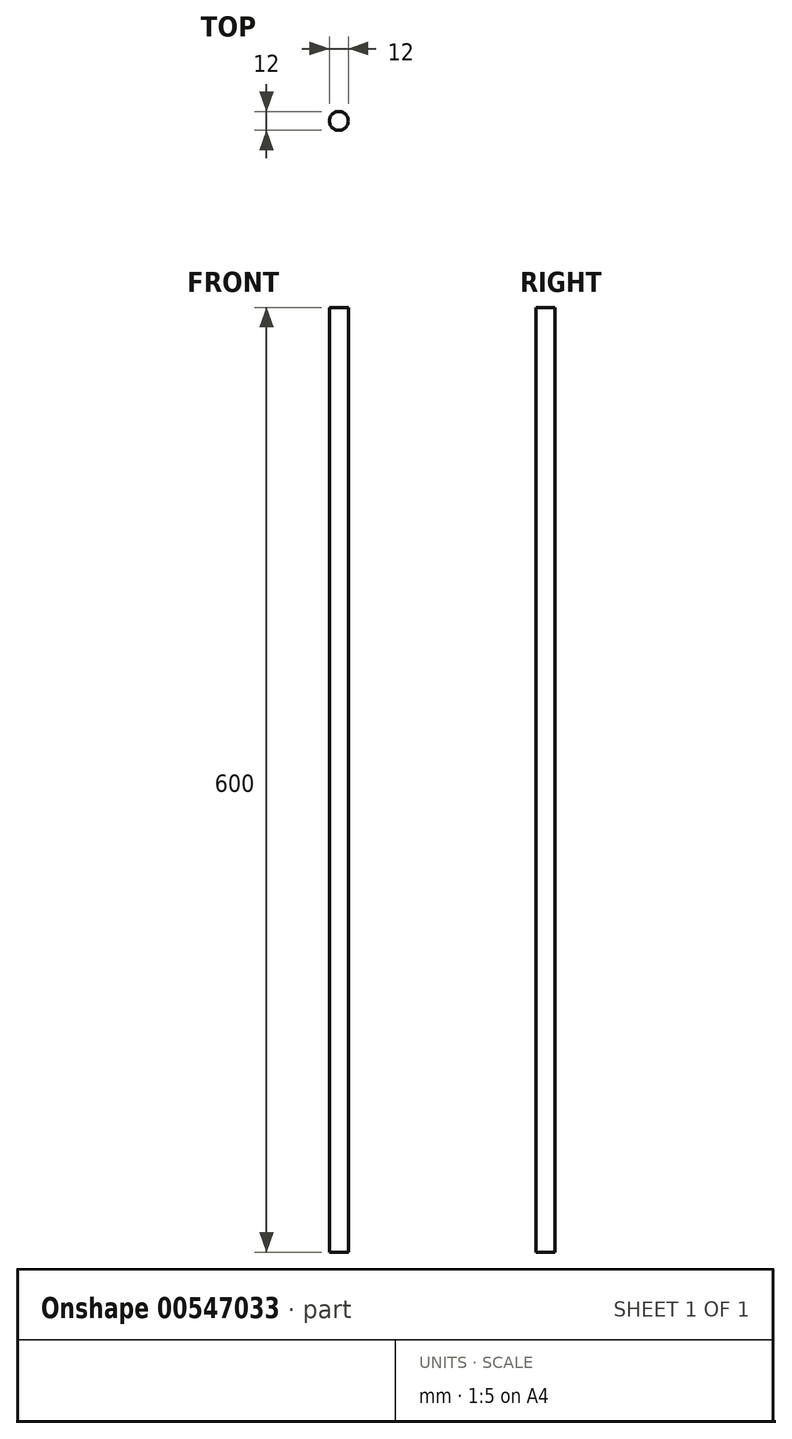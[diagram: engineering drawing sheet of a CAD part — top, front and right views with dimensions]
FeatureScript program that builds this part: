
annotation { "Feature Type Name" : "Feature", "Feature Type Description" : "" }
export const myFeature = defineFeature(function(context is Context, id is Id, definition is map)
    precondition{}
    {
        {
            var Q0;
            Q0=qCreatedBy(makeId("Top.planeOp"),FACE);
            var sketch = newSketch(context, id + "F0", { "sketchPlane" : qUnion([Q0])});
            skCircle(sketch, "E0", {"center": v(-62.47, -46.75) * mm, "radius": 6 * mm});
            skSolve(sketch);
        }
        {
            var Q0;
            Q0=makeQuery(id+"F0.imprint","IMPRINT",FACE,{"disambiguationData":[TD([[makeQuery(id+"F0.imprint","IMPRINT",EDGE,{"derivedFrom":sQuery(id+"F0.wireOp",EDGE,"E0")}),1.0]])]});
            extrude(context, id + "F1", {"entities" : qUnion([Q0]), "depth" : 600 * mm, "offsetDistance" : 25 * mm});
        }
    });
